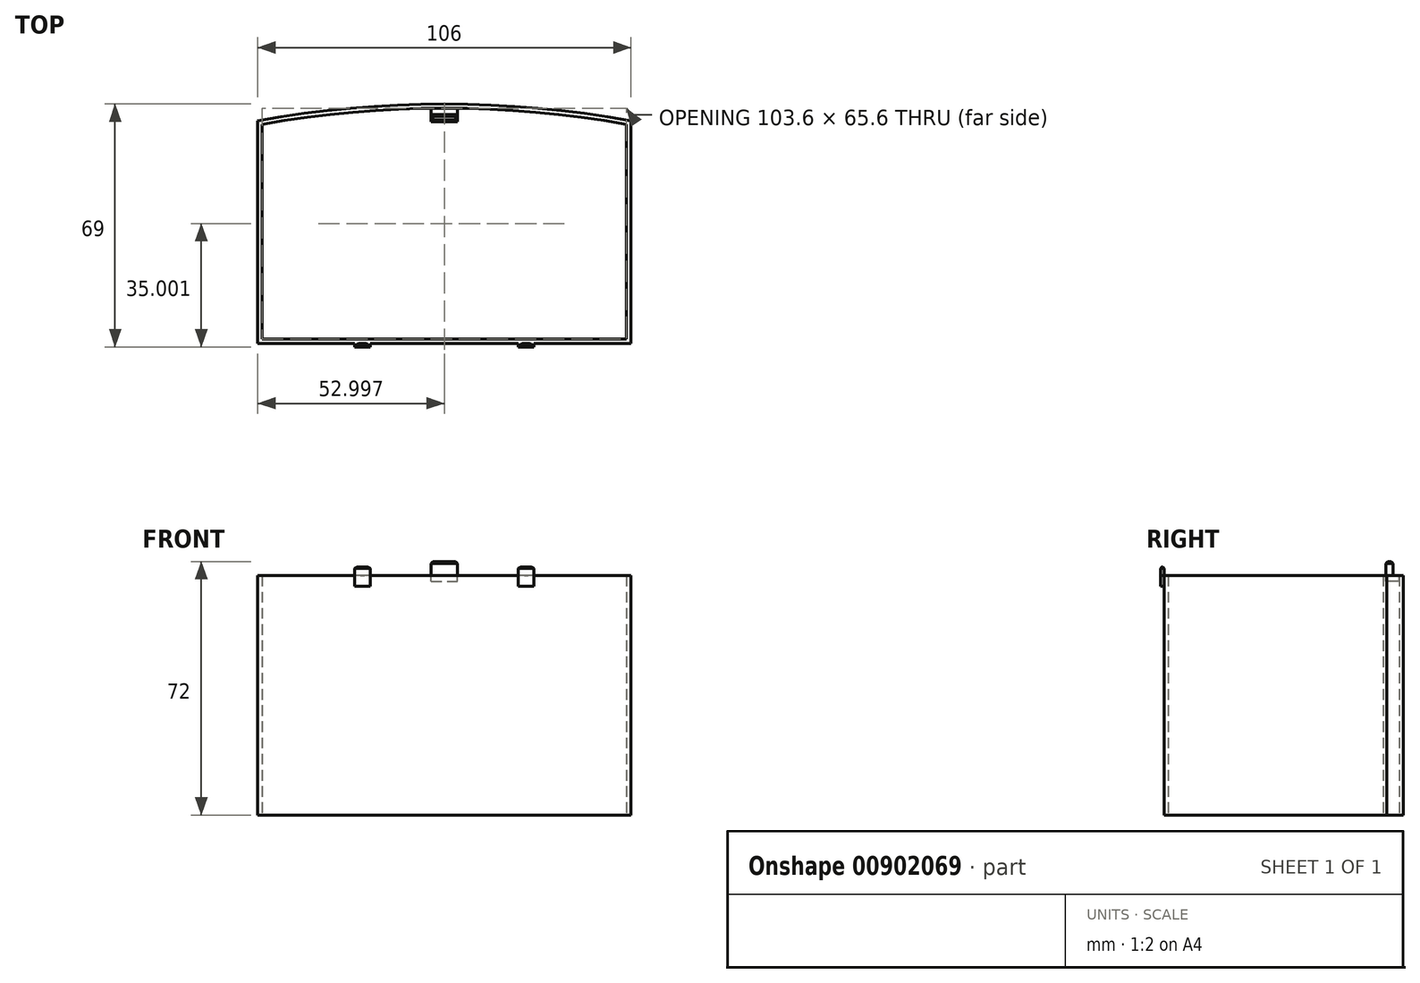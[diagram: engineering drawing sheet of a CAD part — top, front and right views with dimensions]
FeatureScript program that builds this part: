
annotation { "Feature Type Name" : "Feature", "Feature Type Description" : "" }
export const myFeature = defineFeature(function(context is Context, id is Id, definition is map)
    precondition{}
    {
        {
            var Q0;
            Q0=qCreatedBy(makeId("Top.planeOp"),FACE);
            var sketch = newSketch(context, id + "F0", { "sketchPlane" : qUnion([Q0])});
            skLineSegment(sketch, "E0.left", {"start": v(-44.25, 10.97) * mm, "end": v(-44.25, -52.23) * mm});
            skLineSegment(sketch, "E0.right", {"start": v(61.75, 10.97) * mm, "end": v(61.75, -52.23) * mm});
            skPoint(sketch, "E1.1.internal.snap0", {"position": v(8.75, 10.97) * mm});
            skArc(sketch, "E2", {"start": v(61.75, 10.97) * mm, "mid": v(8.75, 15.77) * mm, "end": v(-44.25, 10.97) * mm});
            skLineSegment(sketch, "E3", {"start": v(-44.25, -52.23) * mm, "end": v(61.75, -52.23) * mm});
            skArc(sketch, "E4.0", {"start": v(60.55, 9.97) * mm, "mid": v(8.75, 14.57) * mm, "end": v(-43.05, 9.97) * mm});
            skLineSegment(sketch, "E4.1", {"start": v(60.55, 9.97) * mm, "end": v(60.55, -51.03) * mm});
            skLineSegment(sketch, "E4.2", {"start": v(-43.05, -51.03) * mm, "end": v(60.55, -51.03) * mm});
            skLineSegment(sketch, "E4.3", {"start": v(-43.05, 9.97) * mm, "end": v(-43.05, -51.03) * mm});
            skSolve(sketch);
        }
        {
            var Q0;
            Q0=makeQuery(id+"F0.imprint","IMPRINT",FACE,{"disambiguationData":[TD([[makeQuery(id+"F0.imprint","IMPRINT",EDGE,{"derivedFrom":sQuery(id+"F0.wireOp",EDGE,"E0.left")}),1.0]])]});
            extrude(context, id + "F1", {"entities" : qUnion([Q0]), "depth" : 68 * mm, "offsetDistance" : 25 * mm});
        }
        {
            var Q0;
            Q0=makeQuery(id+"F1.opExtrude","SWEPT_FACE",FACE,{"disambiguationData":[OSD([sQuery(id+"F0.wireOp",EDGE,"E3")])]});
            var sketch = newSketch(context, id + "F2", { "sketchPlane" : qUnion([Q0])});
            skLineSegment(sketch, "E5.bottom", {"start": v(-16.75, 65) * mm, "end": v(-12.25, 65) * mm});
            skLineSegment(sketch, "E5.top", {"start": v(-16.75, 70.5) * mm, "end": v(-12.25, 70.5) * mm});
            skLineSegment(sketch, "E5.left", {"start": v(-16.75, 65) * mm, "end": v(-16.75, 70.5) * mm});
            skLineSegment(sketch, "E5.right", {"start": v(-12.25, 65) * mm, "end": v(-12.25, 70.5) * mm});
            skLineSegment(sketch, "E6.bottom", {"start": v(29.75, 65) * mm, "end": v(34.25, 65) * mm});
            skLineSegment(sketch, "E6.top", {"start": v(29.75, 70.5) * mm, "end": v(34.25, 70.5) * mm});
            skLineSegment(sketch, "E6.left", {"start": v(29.75, 65) * mm, "end": v(29.75, 70.5) * mm});
            skLineSegment(sketch, "E6.right", {"start": v(34.25, 65) * mm, "end": v(34.25, 70.5) * mm});
            skSolve(sketch);
        }
        {
            var Q0;
            {var subQ0=sQuery(id+"F2.wireOp",EDGE,"E5.top");Q0=makeQuery(id+"F2.imprint","IMPRINT",FACE,{"disambiguationData":[TD([[makeQuery(id+"F2.imprint","IMPRINT",EDGE,{"derivedFrom":subQ0}),-1.0]])]});}
            var Q1;
            {var subQ0=sQuery(id+"F2.wireOp",EDGE,"E6.top");Q1=makeQuery(id+"F2.imprint","IMPRINT",FACE,{"disambiguationData":[TD([[makeQuery(id+"F2.imprint","IMPRINT",EDGE,{"derivedFrom":subQ0}),-1.0]])]});}
            var Q2;
            {var subQ0=sQuery(id+"F2.wireOp",EDGE,"E5.bottom");Q2=makeQuery(id+"F2.imprint","IMPRINT",FACE,{"disambiguationData":[TD([[makeQuery(id+"F2.imprint","IMPRINT",EDGE,{"derivedFrom":subQ0}),1.0]])]});}
            var Q3;
            {var subQ0=sQuery(id+"F2.wireOp",EDGE,"E6.bottom");Q3=makeQuery(id+"F2.imprint","IMPRINT",FACE,{"disambiguationData":[TD([[makeQuery(id+"F2.imprint","IMPRINT",EDGE,{"derivedFrom":subQ0}),1.0]])]});}
            extrude(context, id + "F3", {"entities" : qUnion([Q0, Q1, Q2, Q3]), "operationType" : NewBodyOperationType.ADD, "depth" : 1 * mm, "offsetDistance" : 25 * mm});
        }
        {
            var Q0;
            {var subQ0=sQuery(id+"F2.wireOp",EDGE,"E5.right");Q0=makeQuery(id+"F3.boolean.opBoolean","SPLIT",EDGE,{"disambiguationData":[topologyDisambiguationEdgeConnected([makeQuery(id+"F1.opExtrude","SWEPT_FACE",FACE,{"disambiguationData":[OSD([sQuery(id+"F0.wireOp",EDGE,"E3")])]})])],"derivedFrom":makeQuery(id+"F3.opExtrude","CAP_EDGE",EDGE,{"disambiguationData":[OSD([subQ0])],"isStart":true})});}
            var Q1;
            {var subQ0=sQuery(id+"F2.wireOp",EDGE,"E5.left");Q1=makeQuery(id+"F3.boolean.opBoolean","SPLIT",EDGE,{"disambiguationData":[topologyDisambiguationEdgeConnected([makeQuery(id+"F1.opExtrude","SWEPT_FACE",FACE,{"disambiguationData":[OSD([sQuery(id+"F0.wireOp",EDGE,"E3")])]})])],"derivedFrom":makeQuery(id+"F3.opExtrude","CAP_EDGE",EDGE,{"disambiguationData":[OSD([subQ0])],"isStart":true})});}
            var Q2;
            Q2=makeQuery(id+"F3.opExtrude","CAP_EDGE",EDGE,{"disambiguationData":[OSD([sQuery(id+"F2.wireOp",EDGE,"E5.bottom")])],"isStart":true});
            var Q3;
            {var subQ0=sQuery(id+"F2.wireOp",EDGE,"E6.left");Q3=makeQuery(id+"F3.boolean.opBoolean","SPLIT",EDGE,{"disambiguationData":[topologyDisambiguationEdgeConnected([makeQuery(id+"F1.opExtrude","SWEPT_FACE",FACE,{"disambiguationData":[OSD([sQuery(id+"F0.wireOp",EDGE,"E3")])]})])],"derivedFrom":makeQuery(id+"F3.opExtrude","CAP_EDGE",EDGE,{"disambiguationData":[OSD([subQ0])],"isStart":true})});}
            var Q4;
            Q4=makeQuery(id+"F3.opExtrude","CAP_EDGE",EDGE,{"disambiguationData":[OSD([sQuery(id+"F2.wireOp",EDGE,"E6.bottom")])],"isStart":true});
            var Q5;
            {var subQ0=sQuery(id+"F2.wireOp",EDGE,"E6.right");Q5=makeQuery(id+"F3.boolean.opBoolean","SPLIT",EDGE,{"disambiguationData":[topologyDisambiguationEdgeConnected([makeQuery(id+"F1.opExtrude","SWEPT_FACE",FACE,{"disambiguationData":[OSD([sQuery(id+"F0.wireOp",EDGE,"E3")])]})])],"derivedFrom":makeQuery(id+"F3.opExtrude","CAP_EDGE",EDGE,{"disambiguationData":[OSD([subQ0])],"isStart":true})});}
            fillet(context, id + "F4", {"entities" : qUnion([Q0, Q1, Q2, Q3, Q4, Q5]), "radius" : 2 * mm, "tangentPropagation" : true, "allowEdgeOverflow" : false});
        }
        {
            var Q0;
            Q0=makeQuery(id+"F1.opExtrude","CAP_FACE",FACE,{"disambiguationData":[OSD([sQuery(id+"F0.wireOp",EDGE,"E0.left"),sQuery(id+"F0.wireOp",EDGE,"E0.right"),sQuery(id+"F0.wireOp",EDGE,"E2"),sQuery(id+"F0.wireOp",EDGE,"E3"),sQuery(id+"F0.wireOp",EDGE,"E4.0"),sQuery(id+"F0.wireOp",EDGE,"E4.1"),sQuery(id+"F0.wireOp",EDGE,"E4.2"),sQuery(id+"F0.wireOp",EDGE,"E4.3")])],"isStart":false});
            var sketch = newSketch(context, id + "F5", { "sketchPlane" : qUnion([Q0])});
            skLineSegment(sketch, "E7.bottom", {"start": v(5, 14.55) * mm, "end": v(12.5, 14.55) * mm});
            skLineSegment(sketch, "E7.top", {"start": v(5, 10.75) * mm, "end": v(12.5, 10.75) * mm});
            skLineSegment(sketch, "E7.left", {"start": v(5, 14.55) * mm, "end": v(5, 10.75) * mm});
            skLineSegment(sketch, "E7.right", {"start": v(12.5, 14.55) * mm, "end": v(12.5, 10.75) * mm});
            skSolve(sketch);
        }
        {
            var Q0;
            Q0=makeQuery(id+"F5.imprint","IMPRINT",FACE,{"disambiguationData":[TD([[makeQuery(id+"F5.imprint","IMPRINT",EDGE,{"derivedFrom":sQuery(id+"F5.wireOp",EDGE,"E7.bottom")}),-1.0]])]});
            extrude(context, id + "F6", {"entities" : qUnion([Q0]), "depth" : -1.6 * mm, "offsetDistance" : 25 * mm});
        }
        {
            var Q0;
            Q0=makeQuery(id+"F6.opExtrude","CAP_FACE",FACE,{"disambiguationData":[OSD([sQuery(id+"F5.wireOp",EDGE,"E7.bottom"),sQuery(id+"F5.wireOp",EDGE,"E7.top"),sQuery(id+"F5.wireOp",EDGE,"E7.left"),sQuery(id+"F5.wireOp",EDGE,"E7.right")])],"isStart":true});
            var sketch = newSketch(context, id + "F7", { "sketchPlane" : qUnion([Q0])});
            skLineSegment(sketch, "E8.bottom", {"start": v(5, 10.75) * mm, "end": v(12.5, 10.75) * mm});
            skLineSegment(sketch, "E8.top", {"start": v(5, 12.75) * mm, "end": v(12.5, 12.75) * mm});
            skLineSegment(sketch, "E8.left", {"start": v(5, 10.75) * mm, "end": v(5, 12.75) * mm});
            skLineSegment(sketch, "E8.right", {"start": v(12.5, 10.75) * mm, "end": v(12.5, 12.75) * mm});
            skSolve(sketch);
        }
        {
            var Q0;
            Q0 = qSketchRegion(id + "F7", true);
            extrude(context, id + "F8", {"entities" : qUnion([Q0]), "operationType" : NewBodyOperationType.ADD, "depth" : 4 * mm, "offsetDistance" : 25 * mm});
        }
        {
            var Q0;
            Q0=makeQuery(id+"F8.opExtrude","CAP_EDGE",EDGE,{"disambiguationData":[OSD([sQuery(id+"F7.wireOp",EDGE,"E8.left")])],"isStart":false});
            var Q1;
            Q1=makeQuery(id+"F8.opExtrude","CAP_EDGE",EDGE,{"disambiguationData":[OSD([sQuery(id+"F7.wireOp",EDGE,"E8.bottom")])],"isStart":false});
            var Q2;
            Q2=makeQuery(id+"F8.opExtrude","CAP_EDGE",EDGE,{"disambiguationData":[OSD([sQuery(id+"F7.wireOp",EDGE,"E8.top")])],"isStart":false});
            var Q3;
            Q3=makeQuery(id+"F8.opExtrude","CAP_EDGE",EDGE,{"disambiguationData":[OSD([sQuery(id+"F7.wireOp",EDGE,"E8.right")])],"isStart":false});
            chamfer(context, id + "F9", {"entities" : qUnion([Q0, Q1, Q2, Q3]), "width" : .5 * mm, "tangentPropagation" : true});
        }
        {
            var Q0;
            Q0=makeQuery(id+"F3.opExtrude","CAP_EDGE",EDGE,{"disambiguationData":[OSD([sQuery(id+"F2.wireOp",EDGE,"E6.top")])],"isStart":true});
            var Q1;
            Q1=makeQuery(id+"F3.opExtrude","SWEPT_EDGE",EDGE,{"disambiguationData":[OSD([sQuery(id+"F2.wireOp",EDGE,"E6.top"),sQuery(id+"F2.wireOp",EDGE,"E6.left")])]});
            var Q2;
            Q2=makeQuery(id+"F3.opExtrude","CAP_EDGE",EDGE,{"disambiguationData":[OSD([sQuery(id+"F2.wireOp",EDGE,"E6.top")])],"isStart":false});
            var Q3;
            Q3=makeQuery(id+"F3.opExtrude","SWEPT_EDGE",EDGE,{"disambiguationData":[OSD([sQuery(id+"F2.wireOp",EDGE,"E6.top"),sQuery(id+"F2.wireOp",EDGE,"E6.right")])]});
            var Q4;
            Q4=makeQuery(id+"F3.opExtrude","CAP_EDGE",EDGE,{"disambiguationData":[OSD([sQuery(id+"F2.wireOp",EDGE,"E5.top")])],"isStart":true});
            var Q5;
            Q5=makeQuery(id+"F3.opExtrude","SWEPT_EDGE",EDGE,{"disambiguationData":[OSD([sQuery(id+"F2.wireOp",EDGE,"E5.top"),sQuery(id+"F2.wireOp",EDGE,"E5.left")])]});
            var Q6;
            Q6=makeQuery(id+"F3.opExtrude","SWEPT_EDGE",EDGE,{"disambiguationData":[OSD([sQuery(id+"F2.wireOp",EDGE,"E5.top"),sQuery(id+"F2.wireOp",EDGE,"E5.right")])]});
            var Q7;
            Q7=makeQuery(id+"F3.opExtrude","CAP_EDGE",EDGE,{"disambiguationData":[OSD([sQuery(id+"F2.wireOp",EDGE,"E5.top")])],"isStart":false});
            chamfer(context, id + "F10", {"entities" : qUnion([Q0, Q1, Q2, Q3, Q4, Q5, Q6, Q7]), "width" : .4 * mm, "tangentPropagation" : true});
        }
    });
